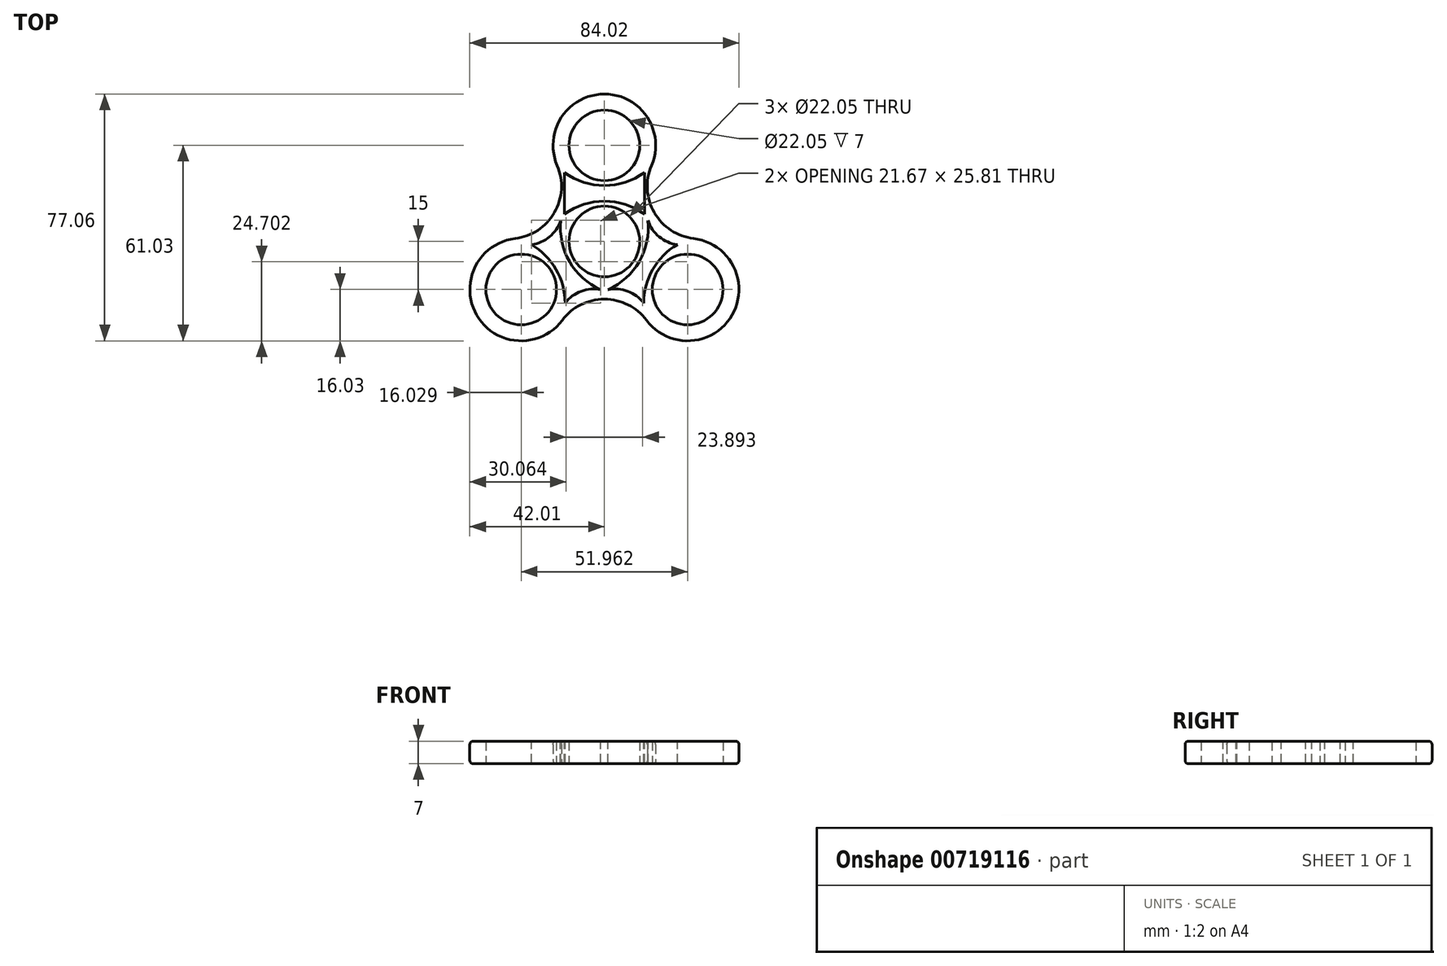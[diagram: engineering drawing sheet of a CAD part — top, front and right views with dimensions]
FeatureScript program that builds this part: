
annotation { "Feature Type Name" : "Feature", "Feature Type Description" : "" }
export const myFeature = defineFeature(function(context is Context, id is Id, definition is map)
    precondition{}
    {
        {
            var Q0;
            Q0=qCreatedBy(makeId("Top.planeOp"),FACE);
            var sketch = newSketch(context, id + "F0", { "sketchPlane" : qUnion([Q0])});
            skCircle(sketch, "E0", {"center": v(0, 0) * mm, "radius": 11.03 * mm});
            skCircle(sketch, "E1", {"center": v(0, 30) * mm, "radius": 11.03 * mm});
            skCircle(sketch, "E2.0", {"center": v(0, 30) * mm, "radius": 16.02 * mm});
            skCircle(sketch, "E3.0", {"center": v(0, 0) * mm, "radius": 18.02 * mm});
            skArc(sketch, "E4", {"start": v(-15.59, 9.05) * mm, "mid": v(-13.42, 16.25) * mm, "end": v(-14.72, 23.66) * mm});
            skLineSegment(sketch, "E5", {"start": v(0, -22.67) * mm, "end": v(0, 73.3) * mm, "construction": true});
            skArc(sketch, "E6.MirrorCS", {"start": v(15.59, 9.05) * mm, "mid": v(13.42, 16.25) * mm, "end": v(14.72, 23.66) * mm});
            skArc(sketch, "E7.1.0", {"start": v(-0.04, -18.02) * mm, "mid": v(-7.36, -19.75) * mm, "end": v(-13.13, -24.58) * mm});
            skArc(sketch, "E7.1.1", {"start": v(-15.63, 8.98) * mm, "mid": v(-20.78, 3.5) * mm, "end": v(-27.85, 0.92) * mm});
            skCircle(sketch, "E7.1.2", {"center": v(-25.98, -15) * mm, "radius": 16.02 * mm});
            skCircle(sketch, "E7.1.3", {"center": v(-25.98, -15) * mm, "radius": 11.03 * mm});
            skArc(sketch, "E7.2.0", {"start": v(15.63, 8.98) * mm, "mid": v(20.78, 3.5) * mm, "end": v(27.85, 0.92) * mm});
            skArc(sketch, "E7.2.1", {"start": v(0.04, -18.02) * mm, "mid": v(7.36, -19.75) * mm, "end": v(13.13, -24.58) * mm});
            skCircle(sketch, "E7.2.2", {"center": v(25.98, -15) * mm, "radius": 16.02 * mm});
            skCircle(sketch, "E7.2.3", {"center": v(25.98, -15) * mm, "radius": 11.03 * mm});
            skSolve(sketch);
        }
        {
            var Q0;
            Q0=qSketchRegion(id+"F0",true);
            var Q1;
            Q1=makeQuery(id+"F0.imprint","IMPRINT",FACE,{"disambiguationData":[TD([[makeQuery(id+"F0.imprint","IMPRINT",EDGE,{"derivedFrom":sQuery(id+"F0.wireOp",EDGE,"E0")}),-1.0]])]});
            var Q2;
            {var subQ0=sQuery(id+"F0.wireOp",EDGE,"E7.1.2");var subQ1=sQuery(id+"F0.wireOp",EDGE,"E3.0");var subQ2=makeQuery(id+"F0.imprint","INTERSECT",VERTEX,{"disambiguationData":[OD(0.0)],"derivedFrom":[subQ1,subQ0]});Q2=makeQuery(id+"F0.imprint","IMPRINT",FACE,{"disambiguationData":[TD([[makeQuery(id+"F0.imprint","IMPRINT",EDGE,{"disambiguationData":[TD([[subQ2,-1.0]])],"derivedFrom":subQ1}),1.0]])]});}
            var Q3;
            {var subQ0=sQuery(id+"F0.wireOp",EDGE,"E3.0");var subQ1=sQuery(id+"F0.wireOp",EDGE,"E2.0");var subQ2=makeQuery(id+"F0.imprint","INTERSECT",VERTEX,{"disambiguationData":[OD(0.0)],"derivedFrom":[subQ1,subQ0]});Q3=makeQuery(id+"F0.imprint","IMPRINT",FACE,{"disambiguationData":[TD([[makeQuery(id+"F0.imprint","IMPRINT",EDGE,{"disambiguationData":[TD([[subQ2,-1.0]])],"derivedFrom":subQ1}),1.0]])]});}
            var Q4;
            {var subQ0=sQuery(id+"F0.wireOp",EDGE,"E7.2.2");var subQ1=sQuery(id+"F0.wireOp",EDGE,"E3.0");var subQ2=makeQuery(id+"F0.imprint","INTERSECT",VERTEX,{"disambiguationData":[OD(0.0)],"derivedFrom":[subQ1,subQ0]});Q4=makeQuery(id+"F0.imprint","IMPRINT",FACE,{"disambiguationData":[TD([[makeQuery(id+"F0.imprint","IMPRINT",EDGE,{"disambiguationData":[TD([[subQ2,-1.0]])],"derivedFrom":subQ1}),1.0]])]});}
            extrude(context, id + "F1", {"entities" : qUnion([Q0, Q1, Q2, Q3, Q4]), "depth" : 7 * mm, "offsetDistance" : 25 * mm});
        }
        {
            var Q0;
            Q0=makeQuery(id+"F1.opExtrude","SWEPT_FACE",FACE,{"disambiguationData":[OSD([sQuery(id+"F0.wireOp",EDGE,"E2.0")])]});
            var Q1;
            Q1=makeQuery(id+"F1.opExtrude","SWEPT_FACE",FACE,{"disambiguationData":[OSD([sQuery(id+"F0.wireOp",EDGE,"E4")])]});
            var Q2;
            Q2=makeQuery(id+"F1.opExtrude","SWEPT_FACE",FACE,{"disambiguationData":[OSD([sQuery(id+"F0.wireOp",EDGE,"E7.1.1")])]});
            var Q3;
            Q3=makeQuery(id+"F1.opExtrude","SWEPT_FACE",FACE,{"disambiguationData":[OSD([sQuery(id+"F0.wireOp",EDGE,"E7.1.2")])]});
            var Q4;
            Q4=makeQuery(id+"F1.opExtrude","SWEPT_FACE",FACE,{"disambiguationData":[OSD([sQuery(id+"F0.wireOp",EDGE,"E7.2.1")])]});
            fillet(context, id + "F2", {"entities" : qUnion([Q0, Q1, Q2, Q3, Q4]), "radius" : 1 * mm, "tangentPropagation" : true, "allowEdgeOverflow" : false});
        }
        {
            var Q0;
            Q0=makeQuery(id+"F1.opExtrude","CAP_FACE",FACE,{"disambiguationData":[OSD([sQuery(id+"F0.wireOp",EDGE,"E0"),sQuery(id+"F0.wireOp",EDGE,"E1"),sQuery(id+"F0.wireOp",EDGE,"E2.0"),sQuery(id+"F0.wireOp",EDGE,"E3.0"),sQuery(id+"F0.wireOp",EDGE,"E4"),sQuery(id+"F0.wireOp",EDGE,"E6.MirrorCS"),sQuery(id+"F0.wireOp",EDGE,"E7.1.0"),sQuery(id+"F0.wireOp",EDGE,"E7.1.1"),sQuery(id+"F0.wireOp",EDGE,"E7.1.2"),sQuery(id+"F0.wireOp",EDGE,"E7.1.3"),sQuery(id+"F0.wireOp",EDGE,"E7.2.0"),sQuery(id+"F0.wireOp",EDGE,"E7.2.1"),sQuery(id+"F0.wireOp",EDGE,"E7.2.2"),sQuery(id+"F0.wireOp",EDGE,"E7.2.3")])],"isStart":false});
            var sketch = newSketch(context, id + "F3", { "sketchPlane" : qUnion([Q0])});
            skPoint(sketch, "E8", {"position": v(0, 0) * mm});
            skLineSegment(sketch, "E9.bottom", {"start": v(12.5, 8.5) * mm, "end": v(-12.5, 8.5) * mm, "construction": true});
            skLineSegment(sketch, "E9.top", {"start": v(12.5, 21.5) * mm, "end": v(-12.5, 21.5) * mm, "construction": true});
            skLineSegment(sketch, "E9.left", {"start": v(12.5, 8.5) * mm, "end": v(12.5, 21.5) * mm});
            skLineSegment(sketch, "E9.right", {"start": v(-12.5, 8.5) * mm, "end": v(-12.5, 21.5) * mm});
            skPoint(sketch, "E9.middle", {"position": v(0, 15) * mm});
            skLineSegment(sketch, "E10", {"start": v(0, 18.97) * mm, "end": v(0, 11.03) * mm, "construction": true});
            skArc(sketch, "E11", {"start": v(12.5, 8.5) * mm, "mid": v(0, 12.56) * mm, "end": v(-12.5, 8.5) * mm});
            skLineSegment(sketch, "E12", {"start": v(-12.5, 15) * mm, "end": v(12.5, 15) * mm, "construction": true});
            skArc(sketch, "E13.MirrorCS", {"start": v(12.5, 21.5) * mm, "mid": v(0, 17.44) * mm, "end": v(-12.5, 21.5) * mm});
            skArc(sketch, "E14", {"start": v(-12.5, 8.5) * mm, "mid": v(-9.74, 14.78) * mm, "end": v(-11.15, 21.5) * mm});
            skArc(sketch, "E15.MirrorCS", {"start": v(12.5, 8.5) * mm, "mid": v(9.74, 14.78) * mm, "end": v(11.15, 21.5) * mm});
            skArc(sketch, "E16.1.0", {"start": v(-13.61, 6.58) * mm, "mid": v(-10.88, -6.28) * mm, "end": v(-1.11, -15.08) * mm});
            skArc(sketch, "E16.1.1", {"start": v(-13.61, 6.58) * mm, "mid": v(-17.67, 1.04) * mm, "end": v(-24.2, -1.1) * mm});
            skArc(sketch, "E16.1.2", {"start": v(-24.87, 0.08) * mm, "mid": v(-15.1, -8.72) * mm, "end": v(-12.37, -21.58) * mm});
            skArc(sketch, "E16.1.3", {"start": v(-1.11, -15.08) * mm, "mid": v(-7.93, -15.82) * mm, "end": v(-13.04, -20.4) * mm});
            skArc(sketch, "E16.2.0", {"start": v(1.11, -15.08) * mm, "mid": v(10.88, -6.28) * mm, "end": v(13.61, 6.58) * mm});
            skArc(sketch, "E16.2.1", {"start": v(1.11, -15.08) * mm, "mid": v(7.93, -15.82) * mm, "end": v(13.04, -20.4) * mm});
            skArc(sketch, "E16.2.2", {"start": v(12.37, -21.58) * mm, "mid": v(15.1, -8.72) * mm, "end": v(24.87, 0.08) * mm});
            skArc(sketch, "E16.2.3", {"start": v(13.61, 6.58) * mm, "mid": v(17.67, 1.04) * mm, "end": v(24.2, -1.1) * mm});
            skSolve(sketch);
        }
        {
            var Q0;
            Q0 = qSketchRegion(id + "F3", true);
            extrude(context, id + "F4", {"entities" : qUnion([Q0]), "operationType" : NewBodyOperationType.REMOVE, "oppositeDirection" : true, "depth" : 25 * mm, "offsetDistance" : 25 * mm});
        }
    });
